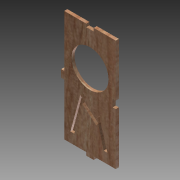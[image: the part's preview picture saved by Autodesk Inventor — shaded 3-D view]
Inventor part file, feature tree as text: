
AUTODESK INVENTOR PART (.ipt)
format: ipt  version: 2015 (Build 190159000, 159)  size: 182,272 bytes
history: native  units: in
note: dims shown in document units (in); Inventor stores cm internally (conversion verified against a paired STEP export)
features: extrude x5, sketch x5
ambient origin geometry x8: Origin, YZ Plane, XZ Plane, XY Plane, X Axis, Y Axis, Z Axis, Center Point
bodies: Solid1 (feature_tree)
feature tree (10):
  extrude  "Extrusion1"  Depth=2.084in
  sketch  "Sketch2"  dims[d2=0.125in d3=0.0in d4=0.15in]
  extrude  "Extrusion2"  Depth=0.15in
  extrude  "Extrusion3"  Depth=0.125in
  sketch  "Sketch3"  dims[d5=0.3in d6=0.125in]
  sketch  "Sketch4"  dims[d7=0.15in d8=0.3in]
  sketch  "Sketch5"  dims[d9=0.125in d13=0.3in d14=0.15in d15=0.125in d16=0.125in d17=0.0in d18=0.125in d19=0.0in d20=0.3in d21=0.15in d22=0.125in d23=1.5in d24=3.0in d25=1.041in d26=0.15in d27=0.15in d29=0.15in d31=75.0deg d32=1.5in d33=0.25in d34=75.0deg d35=0.15in d36=1.15in d38=0.4466in d39=0.2in d40=1.0in d41=0.0in d42=0.1in d43=0.0in]
  extrude  "Extrusion4"  Depth=0.3in
  extrude  "Extrusion5"  Depth=0.3in
  sketch  "Sketch1"  dims[d0=4.5in d1=2.084in]
